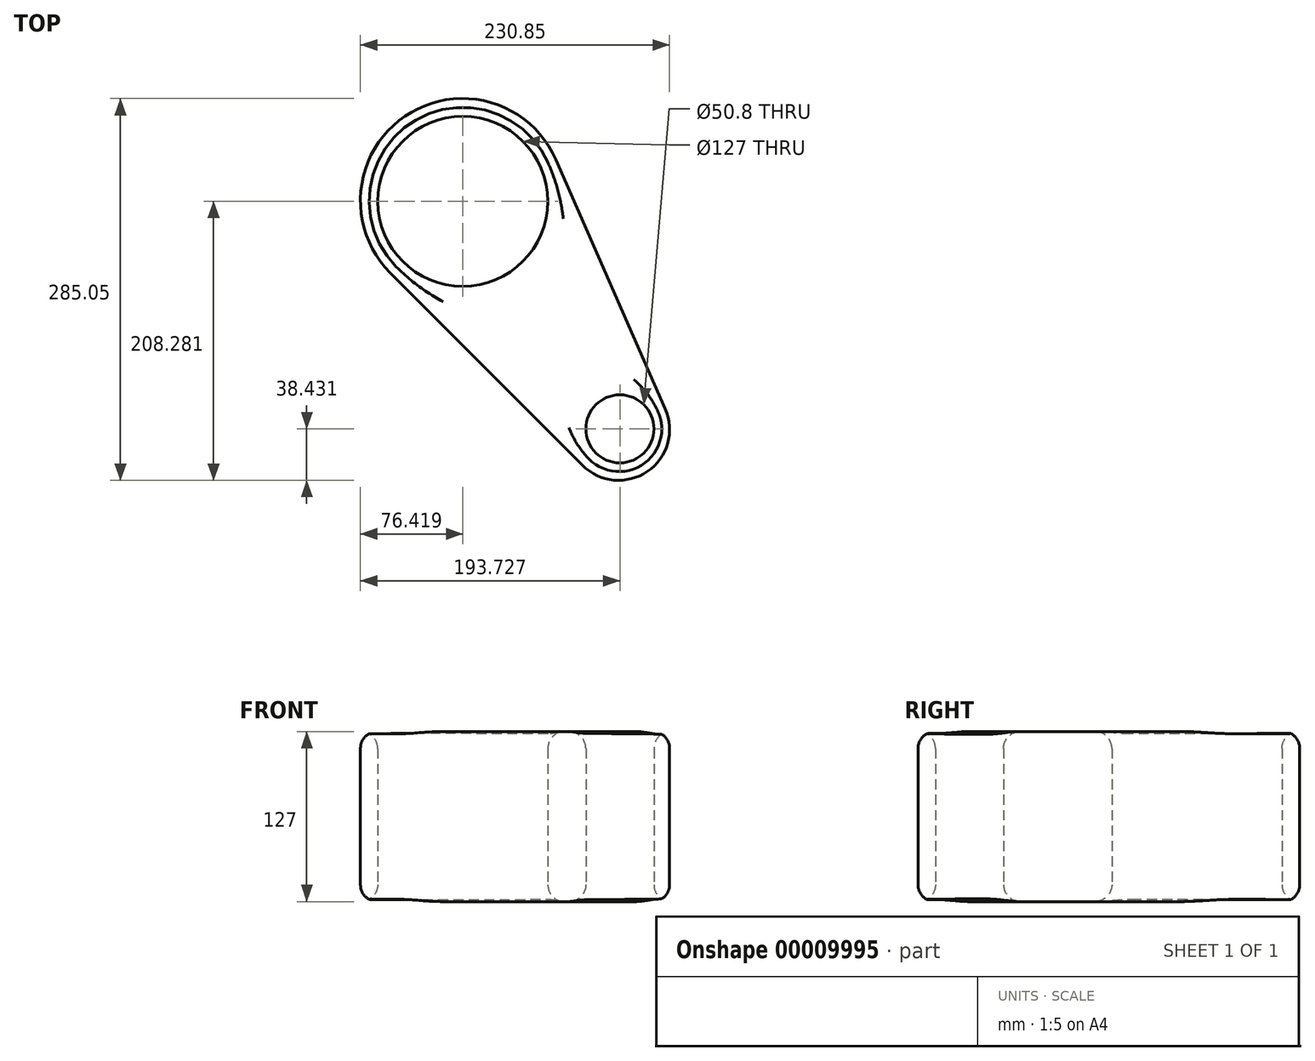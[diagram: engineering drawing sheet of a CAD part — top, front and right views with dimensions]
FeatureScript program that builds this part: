
annotation { "Feature Type Name" : "Feature", "Feature Type Description" : "" }
export const myFeature = defineFeature(function(context is Context, id is Id, definition is map)
    precondition{}
    {
        {
            var Q0;
            Q0=qCreatedBy(makeId("Top.planeOp"),FACE);
            var sketch = newSketch(context, id + "F0", { "sketchPlane" : qUnion([Q0])});
            skCircle(sketch, "E0", {"center": v(-69.77, 125.38) * mm, "radius": 76.2 * mm});
            skCircle(sketch, "E1", {"center": v(46.78, -45.37) * mm, "radius": 38.1 * mm});
            skLineSegment(sketch, "E2", {"start": v(0, 156) * mm, "end": v(81.67, -30.06) * mm});
            skLineSegment(sketch, "E3", {"start": v(-123.71, 71.56) * mm, "end": v(19.82, -72.28) * mm});
            skSolve(sketch);
        }
        {
            var Q0;
            Q0 = qSketchRegion(id + "F0", true);
            extrude(context, id + "F1", {"entities" : qUnion([Q0]), "depth" : 127 * mm});
        }
        {
            var Q0;
            {var subQ0=sQuery(id+"F0.wireOp",EDGE,"E0");var subQ2=makeQuery(id+"F0.imprint","INTERSECT",VERTEX,{"derivedFrom":[subQ0,sQuery(id+"F0.wireOp",EDGE,"E2")]});Q0=makeQuery(id+"F0.imprint","IMPRINT",FACE,{"disambiguationData":[TD([[makeQuery(id+"F0.imprint","IMPRINT",EDGE,{"disambiguationData":[TD([[subQ2,-1.0]])],"derivedFrom":subQ0}),1.0]])]});}
            var sketch = newSketch(context, id + "F2", { "sketchPlane" : qUnion([Q0])});
            skCircle(sketch, "E4", {"center": v(47.76, -45.04) * mm, "radius": 25.4 * mm});
            skSolve(sketch);
        }
        {
            var Q0;
            Q0=makeQuery(id+"F2.imprint","IMPRINT",FACE,{"disambiguationData":[TD([[makeQuery(id+"F2.imprint","IMPRINT",EDGE,{"derivedFrom":sQuery(id+"F2.wireOp",EDGE,"E4")}),1.0]])]});
            extrude(context, id + "F3", {"entities" : qUnion([Q0]), "operationType" : NewBodyOperationType.REMOVE, "depth" : 191.56 * mm});
        }
        {
            var Q0;
            {var subQ0=sQuery(id+"F0.wireOp",EDGE,"E0");var subQ2=makeQuery(id+"F0.imprint","INTERSECT",VERTEX,{"derivedFrom":[subQ0,sQuery(id+"F0.wireOp",EDGE,"E2")]});Q0=makeQuery(id+"F0.imprint","IMPRINT",FACE,{"disambiguationData":[TD([[makeQuery(id+"F0.imprint","IMPRINT",EDGE,{"disambiguationData":[TD([[subQ2,-1.0]])],"derivedFrom":subQ0}),1.0]])]});}
            var sketch = newSketch(context, id + "F4", { "sketchPlane" : qUnion([Q0])});
            skCircle(sketch, "E5", {"center": v(-69.55, 124.81) * mm, "radius": 63.5 * mm});
            skSolve(sketch);
        }
        {
            var Q0;
            Q0=makeQuery(id+"F4.imprint","IMPRINT",FACE,{"disambiguationData":[TD([[makeQuery(id+"F4.imprint","IMPRINT",EDGE,{"derivedFrom":sQuery(id+"F4.wireOp",EDGE,"E5")}),1.0]])]});
            extrude(context, id + "F5", {"entities" : qUnion([Q0]), "operationType" : NewBodyOperationType.REMOVE, "depth" : 392.72 * mm});
        }
        {
            var Q0;
            Q0=makeQuery(id+"F1.opExtrude","CAP_FACE",FACE,{"disambiguationData":[OSD([sQuery(id+"F0.wireOp",EDGE,"E0"),sQuery(id+"F0.wireOp",EDGE,"E1"),sQuery(id+"F0.wireOp",EDGE,"E2"),sQuery(id+"F0.wireOp",EDGE,"E3")])],"isStart":false});
            var Q1;
            Q1=makeQuery(id+"F1.opExtrude","CAP_FACE",FACE,{"disambiguationData":[OSD([sQuery(id+"F0.wireOp",EDGE,"E0"),sQuery(id+"F0.wireOp",EDGE,"E1"),sQuery(id+"F0.wireOp",EDGE,"E2"),sQuery(id+"F0.wireOp",EDGE,"E3")])],"isStart":true});
            fillet(context, id + "F6", {"entities" : qUnion([Q0, Q1]), "radius" : 12.7 * mm, "tangentPropagation" : true, "allowEdgeOverflow" : false});
        }
    });
